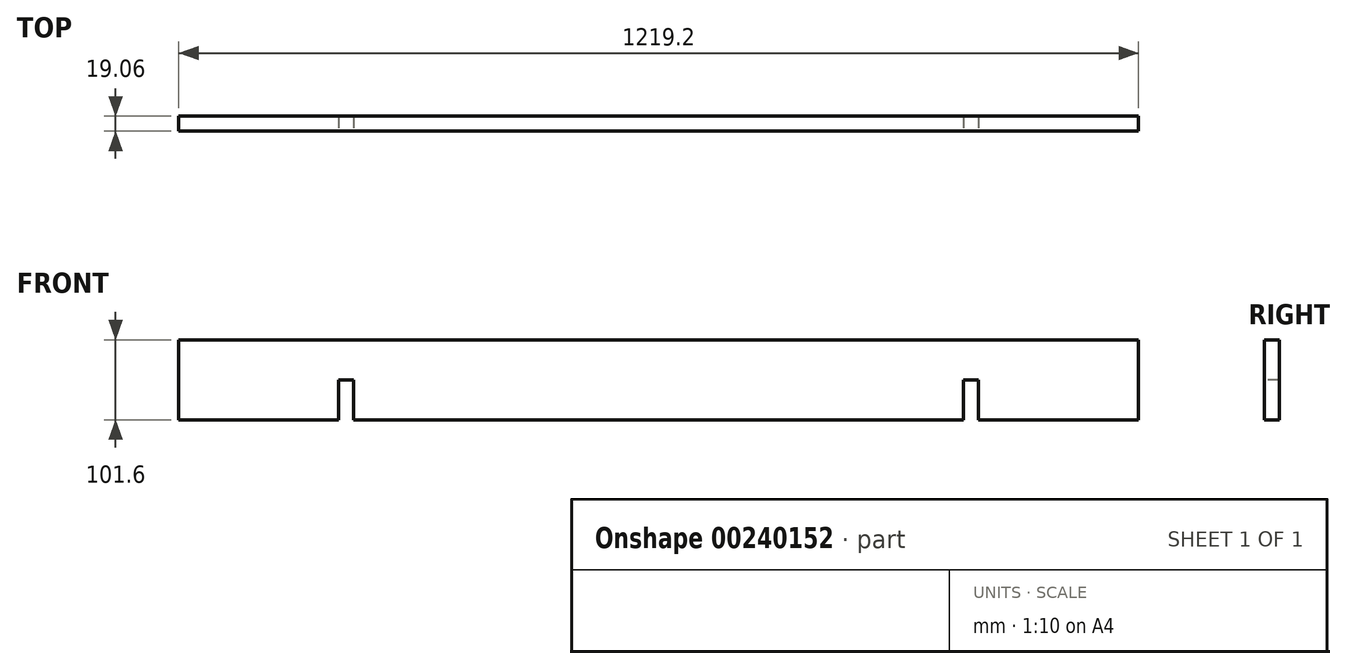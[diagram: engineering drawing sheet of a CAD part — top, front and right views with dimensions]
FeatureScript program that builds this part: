
annotation { "Feature Type Name" : "Feature", "Feature Type Description" : "" }
export const myFeature = defineFeature(function(context is Context, id is Id, definition is map)
    precondition{}
    {
        {
            var Q0;
            Q0=qCreatedBy(makeId("Top.planeOp"),FACE);
            var sketch = newSketch(context, id + "F0", { "sketchPlane" : qUnion([Q0])});
            skLineSegment(sketch, "E0", {"start": v(0, 0) * mm, "end": v(-609.6, 0) * mm});
            skLineSegment(sketch, "E1", {"start": v(609.6, 0) * mm, "end": v(609.6, 9.52) * mm});
            skLineSegment(sketch, "E2", {"start": v(609.6, 9.52) * mm, "end": v(-609.6, 9.52) * mm});
            skLineSegment(sketch, "E3", {"start": v(-609.6, 9.52) * mm, "end": v(-609.6, -9.53) * mm});
            skLineSegment(sketch, "E4", {"start": v(-609.6, -9.53) * mm, "end": v(609.6, -9.53) * mm});
            skLineSegment(sketch, "E5", {"start": v(609.6, -9.52) * mm, "end": v(609.6, 0) * mm});
            skSolve(sketch);
        }
        {
            var Q0;
            Q0 = qSketchRegion(id + "F0", true);
            extrude(context, id + "F1", {"entities" : qUnion([Q0]), "oppositeDirection" : true, "depth" : 101.6 * mm});
        }
        {
            var Q0;
            Q0=makeQuery(id+"F1.opExtrude","SWEPT_FACE",FACE,{"disambiguationData":[OSD([sQuery(id+"F0.wireOp",EDGE,"E4")])]});
            var sketch = newSketch(context, id + "F2", { "sketchPlane" : qUnion([Q0])});
            skLineSegment(sketch, "E6", {"start": v(0, 141.38) * mm, "end": v(0, -251.09) * mm, "construction": true});
            skPoint(sketch, "E6.startSnap0", {"position": v(0, 0) * mm});
            skPoint(sketch, "E6.endSnap0", {"position": v(0, -101.6) * mm});
            skLineSegment(sketch, "E7", {"start": v(0, -144.57) * mm, "end": v(387.35, -144.57) * mm, "construction": true});
            skLineSegment(sketch, "E8", {"start": v(387.35, -144.57) * mm, "end": v(387.35, -101.6) * mm, "construction": true});
            skLineSegment(sketch, "E9", {"start": v(387.35, -101.6) * mm, "end": v(387.35, -50.8) * mm});
            skLineSegment(sketch, "E10", {"start": v(387.35, -50.8) * mm, "end": v(406.4, -50.8) * mm});
            skLineSegment(sketch, "E11", {"start": v(406.4, -50.8) * mm, "end": v(406.4, -101.6) * mm});
            skLineSegment(sketch, "E12", {"start": v(406.4, -101.6) * mm, "end": v(387.35, -101.6) * mm});
            skLineSegment(sketch, "E13.MirrorCS", {"start": v(-387.35, -50.8) * mm, "end": v(-406.4, -50.8) * mm});
            skLineSegment(sketch, "E14.MirrorCS", {"start": v(-387.35, -101.6) * mm, "end": v(-387.35, -50.8) * mm});
            skLineSegment(sketch, "E15.MirrorCS", {"start": v(-406.4, -50.8) * mm, "end": v(-406.4, -101.6) * mm});
            skLineSegment(sketch, "E16.MirrorCS", {"start": v(-406.4, -101.6) * mm, "end": v(-387.35, -101.6) * mm});
            skSolve(sketch);
        }
        {
            var Q0;
            Q0=makeQuery(id+"F2.imprint","IMPRINT",FACE,{"disambiguationData":[TD([[makeQuery(id+"F2.imprint","IMPRINT",EDGE,{"derivedFrom":sQuery(id+"F2.wireOp",EDGE,"E13.MirrorCS")}),1.0]])]});
            var Q1;
            Q1=makeQuery(id+"F2.imprint","IMPRINT",FACE,{"disambiguationData":[TD([[makeQuery(id+"F2.imprint","IMPRINT",EDGE,{"derivedFrom":sQuery(id+"F2.wireOp",EDGE,"E9")}),-1.0]])]});
            extrude(context, id + "F3", {"entities" : qUnion([Q0, Q1]), "operationType" : NewBodyOperationType.REMOVE, "oppositeDirection" : true, "depth" : 25.4 * mm});
        }
    });
